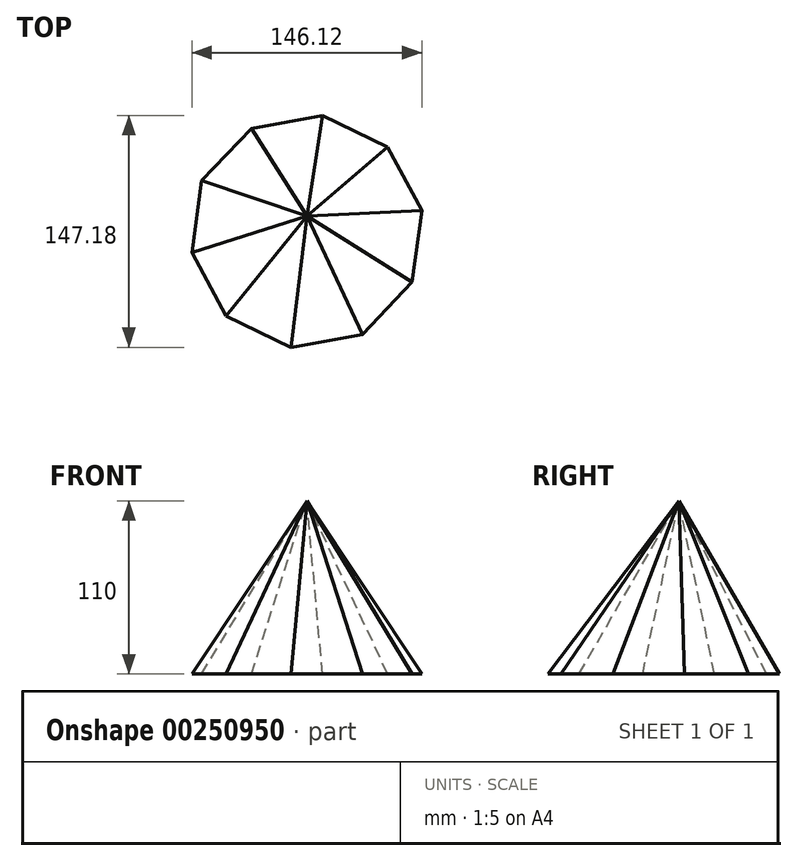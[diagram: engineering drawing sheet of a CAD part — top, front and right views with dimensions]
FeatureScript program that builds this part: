
annotation { "Feature Type Name" : "Feature", "Feature Type Description" : "" }
export const myFeature = defineFeature(function(context is Context, id is Id, definition is map)
    precondition{}
    {
        {
            var Q0;
            Q0=qCreatedBy(makeId("Top.planeOp"),FACE);
            var sketch = newSketch(context, id + "F0", { "sketchPlane" : qUnion([Q0])});
            skCircle(sketch, "E0.cCircle", {"center": v(0, 0) * mm, "radius": 74.26 * mm, "construction": true});
            skLineSegment(sketch, "E0.0", {"start": v(-35.23, 65.37) * mm, "end": v(9.93, 73.6) * mm});
            skLineSegment(sketch, "E0.1", {"start": v(9.93, 73.6) * mm, "end": v(51.29, 53.7) * mm});
            skLineSegment(sketch, "E0.2", {"start": v(51.29, 53.7) * mm, "end": v(73.06, 13.3) * mm});
            skLineSegment(sketch, "E0.3", {"start": v(73.06, 13.3) * mm, "end": v(66.92, -32.18) * mm});
            skLineSegment(sketch, "E0.4", {"start": v(66.92, -32.18) * mm, "end": v(35.23, -65.37) * mm});
            skLineSegment(sketch, "E0.5", {"start": v(35.23, -65.37) * mm, "end": v(-9.93, -73.6) * mm});
            skLineSegment(sketch, "E0.6", {"start": v(-9.93, -73.6) * mm, "end": v(-51.29, -53.7) * mm});
            skLineSegment(sketch, "E0.7", {"start": v(-51.29, -53.7) * mm, "end": v(-73.06, -13.3) * mm});
            skLineSegment(sketch, "E0.8", {"start": v(-73.06, -13.3) * mm, "end": v(-66.92, 32.18) * mm});
            skLineSegment(sketch, "E0.9", {"start": v(-66.92, 32.18) * mm, "end": v(-35.23, 65.37) * mm});
            skSolve(sketch);
        }
        {
            var Q0;
            Q0=qCreatedBy(makeId("Top.planeOp"),FACE);
            cPlane(context, id + "F1", {"entities" : qUnion([Q0]), "cplaneType" : CPlaneType.OFFSET, "offset" : 110 * mm, "width" : 150 * mm, "height" : 150 * mm});
        }
        {
            var Q0;
            Q0=qCreatedBy(id+"F1.planeOp",FACE);
            var sketch = newSketch(context, id + "F2", { "sketchPlane" : qUnion([Q0])});
            skPoint(sketch, "E1", {"position": v(0, 9.61) * mm});
            skSolve(sketch);
        }
        {
            var Q0;
            Q0=makeQuery(id+"F0.imprint","IMPRINT",FACE,{"disambiguationData":[TD([[makeQuery(id+"F0.imprint","IMPRINT",EDGE,{"derivedFrom":sQuery(id+"F0.wireOp",EDGE,"E0.0")}),-1.0]])]});
            var Q1;
            Q1=sQuery(id+"F2.wireOp",VERTEX,"E1");
            loft(context, id + "F3", {"sheetProfilesArray" : [{ "sheetProfileEntities" : qUnion([Q0]) }, { "sheetProfileEntities" : qUnion([Q1]) }]});
        }
    });
